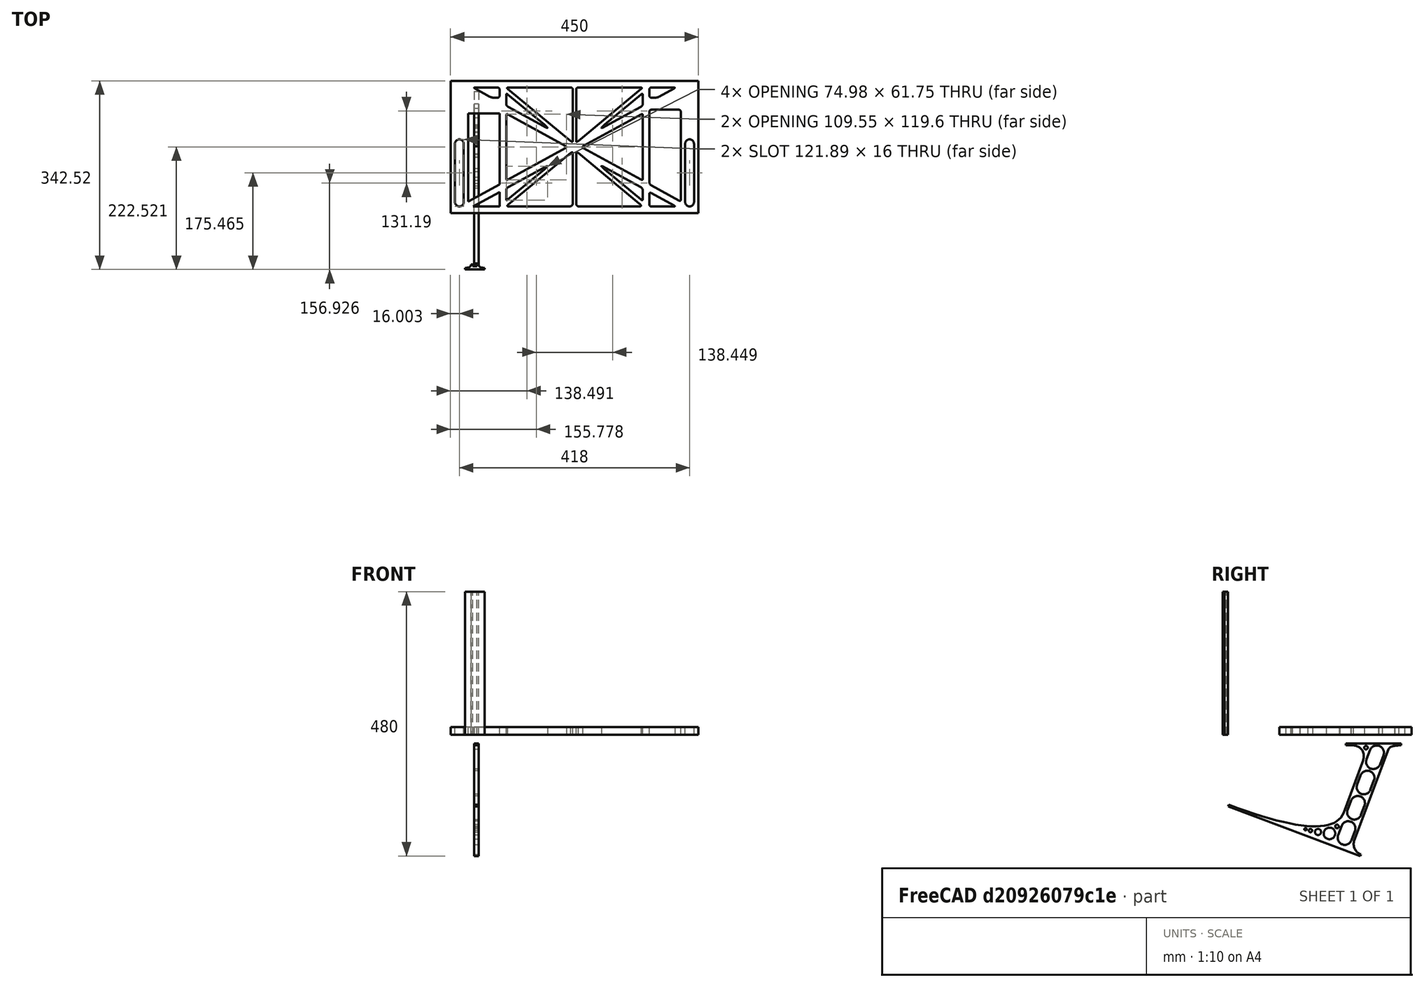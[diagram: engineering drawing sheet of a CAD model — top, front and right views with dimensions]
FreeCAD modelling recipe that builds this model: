
FCSTD DOCUMENT  (FreeCAD 0.19R0.19.2)
Label: laptopStand120FCStd
License: All rights reserved
LicenseURL: http://en.wikipedia.org/wiki/All_rights_reserved
objects: Sketcher::SketchObject×3, Part::Extrusion×3
note: 6 computed .brp shape members not serialized (recipe doc carries the construction recipe); baked Part::Feature solids carry a one-line shape summary decoded from their .brp

FEATURE [Sketcher::SketchObject] Sketch
  FullyConstrained = false
  sketch-geometry (339):
    g0: LineSegment StartX=-10.9272 StartY=-82.7794 StartZ=0 EndX=46.0728 EndY=-51.4823 EndZ=0
    g1: LineSegment StartX=-10.9272 StartY=77.3346 StartZ=0 EndX=-10.9272 EndY=-82.7794 EndZ=0
    g2: LineSegment StartX=-1.92719 StartY=-91.7794 StartZ=0 EndX=46.0728 EndY=-91.7794 EndZ=0
    g3: LineSegment StartX=46.0728 StartY=-65.424 StartZ=0 EndX=-1.92719 EndY=-91.7794 EndZ=0
    g4: LineSegment StartX=46.0728 StartY=-65.424 StartZ=0 EndX=46.0728 EndY=-91.7794 EndZ=0
    g5: LineSegment StartX=46.0728 StartY=77.3346 StartZ=0 EndX=46.0728 EndY=-51.4823 EndZ=0
    g6: LineSegment StartX=-42.9272 StartY=136.221 StartZ=0 EndX=-42.9272 EndY=-103.779 EndZ=0
    g7: LineSegment StartX=407.073 StartY=136.221 StartZ=0 EndX=407.073 EndY=-103.779 EndZ=0
    g8: ArcOfCircle CenterX=-26.9272 CenterY=22.1087 CenterZ=0 NormalX=0 NormalY=0 NormalZ=1 AngleXU=0 Radius=8 StartAngle=1e-16 EndAngle=3.14159
    g9: ArcOfCircle CenterX=-26.9272 CenterY=-83.7794 CenterZ=0 NormalX=0 NormalY=0 NormalZ=1 AngleXU=0 Radius=8 StartAngle=3.14159 EndAngle=6.28319
    g10: LineSegment StartX=-34.9272 StartY=22.1087 StartZ=0 EndX=-34.9272 EndY=-83.7794 EndZ=0
    g11: LineSegment StartX=-18.9272 StartY=22.1087 StartZ=0 EndX=-18.9272 EndY=-83.7794 EndZ=0
    g12: ArcOfCircle CenterX=391.073 CenterY=22.1087 CenterZ=0 NormalX=0 NormalY=0 NormalZ=1 AngleXU=0 Radius=8 StartAngle=-4.4e-15 EndAngle=3.14159
    g13: LineSegment StartX=399.073 StartY=22.1087 StartZ=0 EndX=399.073 EndY=-83.7794 EndZ=0
    g14: LineSegment StartX=383.073 StartY=22.1087 StartZ=0 EndX=383.073 EndY=-83.7794 EndZ=0
    g15: ArcOfCircle CenterX=391.073 CenterY=-83.7794 CenterZ=0 NormalX=0 NormalY=0 NormalZ=1 AngleXU=0 Radius=8 StartAngle=3.14159 EndAngle=6.28319
    g16: Circle CenterX=175.022 CenterY=27.0628 CenterZ=0 NormalX=0 NormalY=0 NormalZ=1 AngleXU=0 Radius=1
    g17: Circle CenterX=179.022 CenterY=24.8665 CenterZ=0 NormalX=0 NormalY=0 NormalZ=1 AngleXU=0 Radius=1
    g18: Circle CenterX=179.022 CenterY=27.0628 CenterZ=0 NormalX=0 NormalY=0 NormalZ=1 AngleXU=0 Radius=1
    g19: BSplineCurve PolesCount=3 KnotsCount=2 Degree=2 IsPeriodic=0
    g20: GeomPoint X=175.022 Y=27.0628 Z=0
    g21: GeomPoint X=179.022 Y=27.0628 Z=0
    g22: Circle CenterX=189.124 CenterY=27.0628 CenterZ=0 NormalX=0 NormalY=0 NormalZ=1 AngleXU=0 Radius=1
    g23: Circle CenterX=185.124 CenterY=24.8665 CenterZ=0 NormalX=0 NormalY=0 NormalZ=1 AngleXU=0 Radius=1
    g24: Circle CenterX=185.124 CenterY=27.0628 CenterZ=0 NormalX=0 NormalY=0 NormalZ=1 AngleXU=0 Radius=1
    g25: BSplineCurve PolesCount=3 KnotsCount=2 Degree=2 IsPeriodic=0
    g26: GeomPoint X=189.124 Y=27.0628 Z=0
    g27: GeomPoint X=185.124 Y=27.0628 Z=0
    g28: Circle CenterX=175.022 CenterY=5.37834 CenterZ=0 NormalX=0 NormalY=0 NormalZ=1 AngleXU=0 Radius=1
    g29: Circle CenterX=179.022 CenterY=7.57463 CenterZ=0 NormalX=0 NormalY=0 NormalZ=1 AngleXU=0 Radius=1
    g30: Circle CenterX=179.022 CenterY=5.34704 CenterZ=0 NormalX=0 NormalY=0 NormalZ=1 AngleXU=0 Radius=1
    g31: BSplineCurve PolesCount=3 KnotsCount=2 Degree=2 IsPeriodic=0
    g32: GeomPoint X=175.022 Y=5.37834 Z=0
    g33: GeomPoint X=179.022 Y=5.34704 Z=0
    g34: Circle CenterX=189.124 CenterY=5.37834 CenterZ=0 NormalX=0 NormalY=0 NormalZ=1 AngleXU=0 Radius=1
    g35: Circle CenterX=185.124 CenterY=7.57463 CenterZ=0 NormalX=0 NormalY=0 NormalZ=1 AngleXU=0 Radius=1
    g36: Circle CenterX=185.124 CenterY=5.34704 CenterZ=0 NormalX=0 NormalY=0 NormalZ=1 AngleXU=0 Radius=1
    g37: BSplineCurve PolesCount=3 KnotsCount=2 Degree=2 IsPeriodic=0
    g38: GeomPoint X=189.124 Y=5.37834 Z=0
    g39: GeomPoint X=185.124 Y=5.34704 Z=0
    g40: Circle CenterX=165.871 CenterY=18.1458 CenterZ=0 NormalX=0 NormalY=0 NormalZ=1 AngleXU=0 Radius=1
    g41: Circle CenterX=169.377 CenterY=16.2206 CenterZ=0 NormalX=0 NormalY=0 NormalZ=1 AngleXU=0 Radius=1
    g42: Circle CenterX=165.871 CenterY=14.2954 CenterZ=0 NormalX=0 NormalY=0 NormalZ=1 AngleXU=0 Radius=1
    g43: BSplineCurve PolesCount=3 KnotsCount=2 Degree=2 IsPeriodic=0
    g44: GeomPoint X=165.871 Y=18.1458 Z=0
    g45: GeomPoint X=165.871 Y=14.2954 Z=0
    g46: Circle CenterX=198.275 CenterY=18.1458 CenterZ=0 NormalX=0 NormalY=0 NormalZ=1 AngleXU=0 Radius=1
    g47: Circle CenterX=194.768 CenterY=16.2206 CenterZ=0 NormalX=0 NormalY=0 NormalZ=1 AngleXU=0 Radius=1
    g48: Circle CenterX=198.275 CenterY=14.2954 CenterZ=0 NormalX=0 NormalY=0 NormalZ=1 AngleXU=0 Radius=1
    g49: BSplineCurve PolesCount=3 KnotsCount=2 Degree=2 IsPeriodic=0
    g50: GeomPoint X=198.275 Y=18.1458 Z=0
    g51: GeomPoint X=198.275 Y=14.2954 Z=0
    g52: LineSegment StartX=407.073 StartY=-103.779 StartZ=0 EndX=-42.9272 EndY=-103.779 EndZ=0
    g53: LineSegment StartX=407.073 StartY=136.221 StartZ=0 EndX=-42.9272 EndY=136.221 EndZ=0
    g54: LineSegment StartX=46.0728 StartY=77.3346 StartZ=0 EndX=-10.9272 EndY=77.3346 EndZ=0
    g55: Circle CenterX=125.607 CenterY=54.1951 CenterZ=0 NormalX=0 NormalY=0 NormalZ=1 AngleXU=0 Radius=1
    g56: Circle CenterX=139.632 CenterY=46.4944 CenterZ=0 NormalX=0 NormalY=0 NormalZ=1 AngleXU=0 Radius=1
    g57: Circle CenterX=127.326 CenterY=56.7187 CenterZ=0 NormalX=0 NormalY=0 NormalZ=1 AngleXU=0 Radius=1
    g58: BSplineCurve PolesCount=3 KnotsCount=2 Degree=2 IsPeriodic=0
    g59: GeomPoint X=125.607 Y=54.1951 Z=0
    g60: GeomPoint X=127.326 Y=56.7187 Z=0
    g61: Circle CenterX=236.821 CenterY=56.7187 CenterZ=0 NormalX=0 NormalY=0 NormalZ=1 AngleXU=0 Radius=1
    g62: Circle CenterX=224.513 CenterY=46.4944 CenterZ=0 NormalX=0 NormalY=0 NormalZ=1 AngleXU=0 Radius=1
    g63: Circle CenterX=238.538 CenterY=54.1951 CenterZ=0 NormalX=0 NormalY=0 NormalZ=1 AngleXU=0 Radius=1
    g64: BSplineCurve PolesCount=3 KnotsCount=2 Degree=2 IsPeriodic=0
    g65: GeomPoint X=236.821 Y=56.7187 Z=0
    g66: GeomPoint X=238.538 Y=54.1951 Z=0
    g67: Circle CenterX=238.538 CenterY=-21.7539 CenterZ=0 NormalX=0 NormalY=0 NormalZ=1 AngleXU=0 Radius=1
    g68: Circle CenterX=224.513 CenterY=-14.0532 CenterZ=0 NormalX=0 NormalY=0 NormalZ=1 AngleXU=0 Radius=1
    g69: Circle CenterX=236.821 CenterY=-24.2775 CenterZ=0 NormalX=0 NormalY=0 NormalZ=1 AngleXU=0 Radius=1
    g70: BSplineCurve PolesCount=3 KnotsCount=2 Degree=2 IsPeriodic=0
    g71: GeomPoint X=238.538 Y=-21.7539 Z=0
    g72: GeomPoint X=236.821 Y=-24.2775 Z=0
    g73: Circle CenterX=125.607 CenterY=-21.7539 CenterZ=0 NormalX=0 NormalY=0 NormalZ=1 AngleXU=0 Radius=1
    g74: Circle CenterX=139.632 CenterY=-14.0532 CenterZ=0 NormalX=0 NormalY=0 NormalZ=1 AngleXU=0 Radius=1
    g75: Circle CenterX=127.325 CenterY=-24.2775 CenterZ=0 NormalX=0 NormalY=0 NormalZ=1 AngleXU=0 Radius=1
    g76: BSplineCurve PolesCount=3 KnotsCount=2 Degree=2 IsPeriodic=0
    g77: GeomPoint X=125.607 Y=-21.7539 Z=0
    g78: GeomPoint X=127.325 Y=-24.2775 Z=0
    g79: Circle CenterX=302.996 CenterY=111.695 CenterZ=0 NormalX=0 NormalY=0 NormalZ=1 AngleXU=0 Radius=1
    g80: Circle CenterX=306.073 CenterY=114.251 CenterZ=0 NormalX=0 NormalY=0 NormalZ=1 AngleXU=0 Radius=1
    g81: Circle CenterX=306.073 CenterY=110.251 CenterZ=0 NormalX=0 NormalY=0 NormalZ=1 AngleXU=0 Radius=1
    g82: BSplineCurve PolesCount=3 KnotsCount=2 Degree=2 IsPeriodic=0
    g83: GeomPoint X=302.996 Y=111.695 Z=0
    g84: GeomPoint X=306.073 Y=110.251 Z=0
    g85: Circle CenterX=306.073 CenterY=95.2763 CenterZ=0 NormalX=0 NormalY=0 NormalZ=1 AngleXU=0 Radius=1
    g86: Circle CenterX=306.073 CenterY=91.2763 CenterZ=0 NormalX=0 NormalY=0 NormalZ=1 AngleXU=0 Radius=1
    g87: Circle CenterX=302.567 CenterY=89.3511 CenterZ=0 NormalX=0 NormalY=0 NormalZ=1 AngleXU=0 Radius=1
    g88: BSplineCurve PolesCount=3 KnotsCount=2 Degree=2 IsPeriodic=0
    g89: GeomPoint X=306.073 Y=95.2763 Z=0
    g90: GeomPoint X=302.567 Y=89.3511 Z=0
    g91: LineSegment StartX=306.073 StartY=110.251 StartZ=0 EndX=306.073 EndY=95.2763 EndZ=0
    g92: LineSegment StartX=302.996 StartY=111.695 StartZ=0 EndX=236.821 EndY=56.7187 EndZ=0
    g93: LineSegment StartX=238.538 StartY=54.1951 StartZ=0 EndX=302.567 EndY=89.3511 EndZ=0
    g94: Circle CenterX=61.1496 CenterY=111.695 CenterZ=0 NormalX=0 NormalY=0 NormalZ=1 AngleXU=0 Radius=1
    g95: Circle CenterX=58.0728 CenterY=114.251 CenterZ=0 NormalX=0 NormalY=0 NormalZ=1 AngleXU=0 Radius=1
    g96: Circle CenterX=58.0728 CenterY=110.251 CenterZ=0 NormalX=0 NormalY=0 NormalZ=1 AngleXU=0 Radius=1
    g97: BSplineCurve PolesCount=3 KnotsCount=2 Degree=2 IsPeriodic=0
    g98: GeomPoint X=61.1496 Y=111.695 Z=0
    g99: GeomPoint X=58.0728 Y=110.251 Z=0
    g100: Circle CenterX=61.5791 CenterY=89.3511 CenterZ=0 NormalX=0 NormalY=0 NormalZ=1 AngleXU=0 Radius=1
    g101: Circle CenterX=58.0728 CenterY=91.2763 CenterZ=0 NormalX=0 NormalY=0 NormalZ=1 AngleXU=0 Radius=1
    g102: Circle CenterX=58.0728 CenterY=95.2763 CenterZ=0 NormalX=0 NormalY=0 NormalZ=1 AngleXU=0 Radius=1
    g103: BSplineCurve PolesCount=3 KnotsCount=2 Degree=2 IsPeriodic=0
    g104: GeomPoint X=61.5791 Y=89.3511 Z=0
    g105: GeomPoint X=58.0728 Y=95.2763 Z=0
    g106: LineSegment StartX=58.0728 StartY=110.251 StartZ=0 EndX=58.0728 EndY=95.2763 EndZ=0
    g107: LineSegment StartX=61.1496 StartY=111.695 StartZ=0 EndX=127.326 EndY=56.7187 EndZ=0
    g108: LineSegment StartX=125.607 StartY=54.1951 StartZ=0 EndX=61.5791 EndY=89.3511 EndZ=0
    g109: Circle CenterX=61.5791 CenterY=-56.9099 CenterZ=0 NormalX=0 NormalY=0 NormalZ=1 AngleXU=0 Radius=1
    g110: Circle CenterX=58.0728 CenterY=-58.8351 CenterZ=0 NormalX=0 NormalY=0 NormalZ=1 AngleXU=0 Radius=1
    g111: Circle CenterX=58.0728 CenterY=-62.8351 CenterZ=0 NormalX=0 NormalY=0 NormalZ=1 AngleXU=0 Radius=1
    g112: BSplineCurve PolesCount=3 KnotsCount=2 Degree=2 IsPeriodic=0
    g113: GeomPoint X=61.5791 Y=-56.9099 Z=0
    g114: GeomPoint X=58.0728 Y=-62.8351 Z=0
    g115: Circle CenterX=58.0728 CenterY=-77.8102 CenterZ=0 NormalX=0 NormalY=0 NormalZ=1 AngleXU=0 Radius=1
    g116: Circle CenterX=58.0728 CenterY=-81.8102 CenterZ=0 NormalX=0 NormalY=0 NormalZ=1 AngleXU=0 Radius=1
    g117: Circle CenterX=61.1496 CenterY=-79.2541 CenterZ=0 NormalX=0 NormalY=0 NormalZ=1 AngleXU=0 Radius=1
    g118: BSplineCurve PolesCount=3 KnotsCount=2 Degree=2 IsPeriodic=0
    g119: GeomPoint X=58.0728 Y=-77.8102 Z=0
    g120: GeomPoint X=61.1496 Y=-79.2541 Z=0
    g121: LineSegment StartX=58.0728 StartY=-62.8351 StartZ=0 EndX=58.0728 EndY=-77.8102 EndZ=0
    g122: LineSegment StartX=61.1496 StartY=-79.2541 StartZ=0 EndX=127.325 EndY=-24.2775 EndZ=0
    g123: LineSegment StartX=125.607 StartY=-21.7539 StartZ=0 EndX=61.5791 EndY=-56.9099 EndZ=0
    g124: Circle CenterX=302.567 CenterY=-56.9099 CenterZ=0 NormalX=0 NormalY=0 NormalZ=1 AngleXU=0 Radius=1
    g125: Circle CenterX=306.073 CenterY=-58.8351 CenterZ=0 NormalX=0 NormalY=0 NormalZ=1 AngleXU=0 Radius=1
    g126: Circle CenterX=306.073 CenterY=-62.8351 CenterZ=0 NormalX=0 NormalY=0 NormalZ=1 AngleXU=0 Radius=1
    g127: BSplineCurve PolesCount=3 KnotsCount=2 Degree=2 IsPeriodic=0
    g128: GeomPoint X=302.567 Y=-56.9099 Z=0
    g129: GeomPoint X=306.073 Y=-62.8351 Z=0
    g130: Circle CenterX=302.996 CenterY=-79.2541 CenterZ=0 NormalX=0 NormalY=0 NormalZ=1 AngleXU=0 Radius=1
    g131: Circle CenterX=306.073 CenterY=-81.8102 CenterZ=0 NormalX=0 NormalY=0 NormalZ=1 AngleXU=0 Radius=1
    g132: Circle CenterX=306.073 CenterY=-77.8102 CenterZ=0 NormalX=0 NormalY=0 NormalZ=1 AngleXU=0 Radius=1
    g133: BSplineCurve PolesCount=3 KnotsCount=2 Degree=2 IsPeriodic=0
    g134: GeomPoint X=302.996 Y=-79.2541 Z=0
    g135: GeomPoint X=306.073 Y=-77.8102 Z=0
    g136: LineSegment StartX=306.073 StartY=-62.8351 StartZ=0 EndX=306.073 EndY=-77.8102 EndZ=0
    g137: LineSegment StartX=302.996 StartY=-79.2541 StartZ=0 EndX=236.821 EndY=-24.2775 EndZ=0
    g138: LineSegment StartX=238.538 StartY=-21.7539 StartZ=0 EndX=302.567 EndY=-56.9099 EndZ=0
    g139: Circle CenterX=61.6457 CenterY=-88.8112 CenterZ=0 NormalX=0 NormalY=0 NormalZ=1 AngleXU=0 Radius=1
    g140: Circle CenterX=58.0728 CenterY=-91.7794 CenterZ=0 NormalX=0 NormalY=0 NormalZ=1 AngleXU=0 Radius=1
    g141: Circle CenterX=63.9135 CenterY=-91.7794 CenterZ=0 NormalX=0 NormalY=0 NormalZ=1 AngleXU=0 Radius=1
    g142: BSplineCurve PolesCount=3 KnotsCount=2 Degree=2 IsPeriodic=0
    g143: GeomPoint X=61.6457 Y=-88.8112 Z=0
    g144: GeomPoint X=63.9135 Y=-91.7794 Z=0
    g145: Circle CenterX=179.022 CenterY=-85.8163 CenterZ=0 NormalX=0 NormalY=0 NormalZ=1 AngleXU=0 Radius=1
    g146: Circle CenterX=179.022 CenterY=-91.7794 CenterZ=0 NormalX=0 NormalY=0 NormalZ=1 AngleXU=0 Radius=1
    g147: Circle CenterX=171.895 CenterY=-91.7794 CenterZ=0 NormalX=0 NormalY=0 NormalZ=1 AngleXU=0 Radius=1
    g148: BSplineCurve PolesCount=3 KnotsCount=2 Degree=2 IsPeriodic=0
    g149: GeomPoint X=179.022 Y=-85.8163 Z=0
    g150: GeomPoint X=171.895 Y=-91.7794 Z=0
    g151: Circle CenterX=185.124 CenterY=-86.2028 CenterZ=0 NormalX=0 NormalY=0 NormalZ=1 AngleXU=0 Radius=1
    g152: Circle CenterX=185.124 CenterY=-91.7794 CenterZ=0 NormalX=0 NormalY=0 NormalZ=1 AngleXU=0 Radius=1
    g153: Circle CenterX=191.747 CenterY=-91.7794 CenterZ=0 NormalX=0 NormalY=0 NormalZ=1 AngleXU=0 Radius=1
    g154: BSplineCurve PolesCount=3 KnotsCount=2 Degree=2 IsPeriodic=0
    g155: GeomPoint X=185.124 Y=-86.2028 Z=0
    g156: GeomPoint X=191.747 Y=-91.7794 Z=0
    g157: Circle CenterX=299.888 CenterY=-86.6413 CenterZ=0 NormalX=0 NormalY=0 NormalZ=1 AngleXU=0 Radius=1
    g158: Circle CenterX=306.073 CenterY=-91.7794 CenterZ=0 NormalX=0 NormalY=0 NormalZ=1 AngleXU=0 Radius=1
    g159: Circle CenterX=298.776 CenterY=-91.7794 CenterZ=0 NormalX=0 NormalY=0 NormalZ=1 AngleXU=0 Radius=1
    g160: BSplineCurve PolesCount=3 KnotsCount=2 Degree=2 IsPeriodic=0
    g161: GeomPoint X=299.888 Y=-86.6413 Z=0
    g162: GeomPoint X=298.776 Y=-91.7794 Z=0
    g163: LineSegment StartX=189.124 StartY=5.37834 StartZ=0 EndX=299.888 EndY=-86.6413 EndZ=0
    g164: LineSegment StartX=298.776 StartY=-91.7794 StartZ=0 EndX=191.747 EndY=-91.7794 EndZ=0
    g165: LineSegment StartX=185.124 StartY=-86.2028 StartZ=0 EndX=185.124 EndY=5.34704 EndZ=0
    g166: LineSegment StartX=179.022 StartY=5.34704 StartZ=0 EndX=179.022 EndY=-85.8163 EndZ=0
    g167: LineSegment StartX=171.895 StartY=-91.7794 StartZ=0 EndX=63.9135 EndY=-91.7794 EndZ=0
    g168: LineSegment StartX=61.6457 StartY=-88.8112 StartZ=0 EndX=175.022 EndY=5.37834 EndZ=0
    g169: Circle CenterX=302.073 CenterY=124.221 CenterZ=0 NormalX=0 NormalY=0 NormalZ=1 AngleXU=0 Radius=1
    g170: Circle CenterX=306.073 CenterY=124.221 CenterZ=0 NormalX=0 NormalY=0 NormalZ=1 AngleXU=0 Radius=1
    g171: Circle CenterX=302.996 CenterY=121.665 CenterZ=0 NormalX=0 NormalY=0 NormalZ=1 AngleXU=0 Radius=1
    g172: BSplineCurve PolesCount=3 KnotsCount=2 Degree=2 IsPeriodic=0
    g173: GeomPoint X=302.073 Y=124.221 Z=0
    g174: GeomPoint X=302.996 Y=121.665 Z=0
    g175: Circle CenterX=189.124 CenterY=124.221 CenterZ=0 NormalX=0 NormalY=0 NormalZ=1 AngleXU=0 Radius=1
    g176: Circle CenterX=185.124 CenterY=124.221 CenterZ=0 NormalX=0 NormalY=0 NormalZ=1 AngleXU=0 Radius=1
    g177: Circle CenterX=185.124 CenterY=120.221 CenterZ=0 NormalX=0 NormalY=0 NormalZ=1 AngleXU=0 Radius=1
    g178: BSplineCurve PolesCount=3 KnotsCount=2 Degree=2 IsPeriodic=0
    g179: GeomPoint X=189.124 Y=124.221 Z=0
    g180: GeomPoint X=185.124 Y=120.221 Z=0
    g181: Circle CenterX=175.022 CenterY=124.221 CenterZ=0 NormalX=0 NormalY=0 NormalZ=1 AngleXU=0 Radius=1
    g182: Circle CenterX=179.022 CenterY=124.221 CenterZ=0 NormalX=0 NormalY=0 NormalZ=1 AngleXU=0 Radius=1
    g183: Circle CenterX=179.022 CenterY=120.221 CenterZ=0 NormalX=0 NormalY=0 NormalZ=1 AngleXU=0 Radius=1
    g184: BSplineCurve PolesCount=3 KnotsCount=2 Degree=2 IsPeriodic=0
    g185: GeomPoint X=175.022 Y=124.221 Z=0
    g186: GeomPoint X=179.022 Y=120.221 Z=0
    g187: Circle CenterX=62.0728 CenterY=124.221 CenterZ=0 NormalX=0 NormalY=0 NormalZ=1 AngleXU=0 Radius=1
    g188: Circle CenterX=58.0728 CenterY=124.221 CenterZ=0 NormalX=0 NormalY=0 NormalZ=1 AngleXU=0 Radius=1
    g189: Circle CenterX=61.1496 CenterY=121.665 CenterZ=0 NormalX=0 NormalY=0 NormalZ=1 AngleXU=0 Radius=1
    g190: BSplineCurve PolesCount=3 KnotsCount=2 Degree=2 IsPeriodic=0
    g191: GeomPoint X=62.0728 Y=124.221 Z=0
    g192: GeomPoint X=61.1496 Y=121.665 Z=0
    g193: LineSegment StartX=62.0728 StartY=124.221 StartZ=0 EndX=175.022 EndY=124.221 EndZ=0
    g194: LineSegment StartX=179.022 StartY=120.221 StartZ=0 EndX=179.022 EndY=27.0628 EndZ=0
    g195: LineSegment StartX=185.124 StartY=27.0628 StartZ=0 EndX=185.124 EndY=120.221 EndZ=0
    g196: LineSegment StartX=189.124 StartY=124.221 StartZ=0 EndX=302.073 EndY=124.221 EndZ=0
    g197: LineSegment StartX=302.996 StartY=121.665 StartZ=0 EndX=189.124 EndY=27.0628 EndZ=0
    g198: LineSegment StartX=175.022 StartY=27.0628 StartZ=0 EndX=61.1496 EndY=121.665 EndZ=0
    g199: Circle CenterX=61.5791 CenterY=75.4095 CenterZ=0 NormalX=0 NormalY=0 NormalZ=1 AngleXU=0 Radius=1
    g200: Circle CenterX=58.0728 CenterY=77.3346 CenterZ=0 NormalX=0 NormalY=0 NormalZ=1 AngleXU=0 Radius=1
    g201: Circle CenterX=58.0728 CenterY=73.3346 CenterZ=0 NormalX=0 NormalY=0 NormalZ=1 AngleXU=0 Radius=1
    g202: BSplineCurve PolesCount=3 KnotsCount=2 Degree=2 IsPeriodic=0
    g203: GeomPoint X=61.5791 Y=75.4095 Z=0
    g204: GeomPoint X=58.0728 Y=73.3346 Z=0
    g205: Circle CenterX=58.0728 CenterY=-40.8935 CenterZ=0 NormalX=0 NormalY=0 NormalZ=1 AngleXU=0 Radius=1
    g206: Circle CenterX=58.0728 CenterY=-44.8935 CenterZ=0 NormalX=0 NormalY=0 NormalZ=1 AngleXU=0 Radius=1
    g207: Circle CenterX=61.5791 CenterY=-42.9683 CenterZ=0 NormalX=0 NormalY=0 NormalZ=1 AngleXU=0 Radius=1
    g208: BSplineCurve PolesCount=3 KnotsCount=2 Degree=2 IsPeriodic=0
    g209: GeomPoint X=58.0728 Y=-40.8935 Z=0
    g210: GeomPoint X=61.5791 Y=-42.9683 Z=0
    g211: LineSegment StartX=61.5791 StartY=-42.9683 StartZ=0 EndX=165.871 EndY=14.2954 EndZ=0
    g212: LineSegment StartX=165.871 StartY=18.1458 StartZ=0 EndX=61.5791 EndY=75.4095 EndZ=0
    g213: LineSegment StartX=58.0728 StartY=73.3346 StartZ=0 EndX=58.0728 EndY=-40.8935 EndZ=0
    g214: Circle CenterX=302.567 CenterY=-42.9683 CenterZ=0 NormalX=0 NormalY=0 NormalZ=1 AngleXU=0 Radius=1
    g215: Circle CenterX=306.073 CenterY=-44.8935 CenterZ=0 NormalX=0 NormalY=0 NormalZ=1 AngleXU=0 Radius=1
    g216: Circle CenterX=306.073 CenterY=-40.8935 CenterZ=0 NormalX=0 NormalY=0 NormalZ=1 AngleXU=0 Radius=1
    g217: BSplineCurve PolesCount=3 KnotsCount=2 Degree=2 IsPeriodic=0
    g218: GeomPoint X=302.567 Y=-42.9683 Z=0
    g219: GeomPoint X=306.073 Y=-40.8935 Z=0
    g220: Circle CenterX=306.073 CenterY=73.3346 CenterZ=0 NormalX=0 NormalY=0 NormalZ=1 AngleXU=0 Radius=1
    g221: Circle CenterX=306.073 CenterY=77.3346 CenterZ=0 NormalX=0 NormalY=0 NormalZ=1 AngleXU=0 Radius=1
    g222: Circle CenterX=302.567 CenterY=75.4095 CenterZ=0 NormalX=0 NormalY=0 NormalZ=1 AngleXU=0 Radius=1
    g223: BSplineCurve PolesCount=3 KnotsCount=2 Degree=2 IsPeriodic=0
    g224: GeomPoint X=306.073 Y=73.3346 Z=0
    g225: GeomPoint X=302.567 Y=75.4095 Z=0
    g226: LineSegment StartX=302.567 StartY=-42.9683 StartZ=0 EndX=198.275 EndY=14.2954 EndZ=0
    g227: LineSegment StartX=198.275 StartY=18.1458 StartZ=0 EndX=302.567 EndY=75.4095 EndZ=0
    g228: LineSegment StartX=306.073 StartY=73.3346 StartZ=0 EndX=306.073 EndY=-40.8935 EndZ=0
    g229: LineSegment StartX=322.073 StartY=105.865 StartZ=0 EndX=328.643 EndY=105.865 EndZ=0
    g230: LineSegment StartX=318.073 StartY=120.221 StartZ=0 EndX=318.073 EndY=109.865 EndZ=0
    g231: LineSegment StartX=336.157 StartY=107.779 StartZ=0 EndX=362.567 EndY=122.294 EndZ=0
    g232: Circle CenterX=362.073 CenterY=124.221 CenterZ=0 NormalX=0 NormalY=0 NormalZ=1 AngleXU=0 Radius=1
    g233: Circle CenterX=366.073 CenterY=124.221 CenterZ=0 NormalX=0 NormalY=0 NormalZ=1 AngleXU=0 Radius=1
    g234: Circle CenterX=362.567 CenterY=122.294 CenterZ=0 NormalX=0 NormalY=0 NormalZ=1 AngleXU=0 Radius=1
    g235: BSplineCurve PolesCount=3 KnotsCount=2 Degree=2 IsPeriodic=0
    g236: GeomPoint X=362.073 Y=124.221 Z=0
    g237: GeomPoint X=362.567 Y=122.294 Z=0
    g238: Circle CenterX=322.073 CenterY=124.221 CenterZ=0 NormalX=0 NormalY=0 NormalZ=1 AngleXU=0 Radius=1
    g239: Circle CenterX=318.073 CenterY=124.221 CenterZ=0 NormalX=0 NormalY=0 NormalZ=1 AngleXU=0 Radius=1
    g240: Circle CenterX=318.073 CenterY=120.221 CenterZ=0 NormalX=0 NormalY=0 NormalZ=1 AngleXU=0 Radius=1
    g241: BSplineCurve PolesCount=3 KnotsCount=2 Degree=2 IsPeriodic=0
    g242: GeomPoint X=322.073 Y=124.221 Z=0
    g243: GeomPoint X=318.073 Y=120.221 Z=0
    g244: Circle CenterX=322.073 CenterY=105.865 CenterZ=0 NormalX=0 NormalY=0 NormalZ=1 AngleXU=0 Radius=1
    g245: Circle CenterX=318.073 CenterY=105.865 CenterZ=0 NormalX=0 NormalY=0 NormalZ=1 AngleXU=0 Radius=1
    g246: Circle CenterX=318.073 CenterY=109.865 CenterZ=0 NormalX=0 NormalY=0 NormalZ=1 AngleXU=0 Radius=1
    g247: BSplineCurve PolesCount=3 KnotsCount=2 Degree=2 IsPeriodic=0
    g248: GeomPoint X=322.073 Y=105.865 Z=0
    g249: GeomPoint X=318.073 Y=109.865 Z=0
    g250: Circle CenterX=336.157 CenterY=107.779 CenterZ=0 NormalX=0 NormalY=0 NormalZ=1 AngleXU=0 Radius=1
    g251: Circle CenterX=332.651 CenterY=105.853 CenterZ=0 NormalX=0 NormalY=0 NormalZ=1 AngleXU=0 Radius=1
    g252: Circle CenterX=328.643 CenterY=105.865 CenterZ=0 NormalX=0 NormalY=0 NormalZ=1 AngleXU=0 Radius=1
    g253: BSplineCurve PolesCount=3 KnotsCount=2 Degree=2 IsPeriodic=0
    g254: GeomPoint X=336.157 Y=107.779 Z=0
    g255: GeomPoint X=328.643 Y=105.865 Z=0
    g256: LineSegment StartX=322.073 StartY=124.221 StartZ=0 EndX=362.073 EndY=124.221 EndZ=0
    g257: Circle CenterX=371.567 CenterY=-80.8644 CenterZ=0 NormalX=0 NormalY=0 NormalZ=1 AngleXU=0 Radius=1
    g258: Circle CenterX=375.073 CenterY=-82.7896 CenterZ=0 NormalX=0 NormalY=0 NormalZ=1 AngleXU=0 Radius=1
    g259: Circle CenterX=375.073 CenterY=-78.7896 CenterZ=0 NormalX=0 NormalY=0 NormalZ=1 AngleXU=0 Radius=1
    g260: BSplineCurve PolesCount=3 KnotsCount=2 Degree=2 IsPeriodic=0
    g261: GeomPoint X=371.567 Y=-80.8644 Z=0
    g262: GeomPoint X=375.073 Y=-78.7896 Z=0
    g263: Circle CenterX=321.579 CenterY=-53.4075 CenterZ=0 NormalX=0 NormalY=0 NormalZ=1 AngleXU=0 Radius=1
    g264: Circle CenterX=318.073 CenterY=-51.4823 CenterZ=0 NormalX=0 NormalY=0 NormalZ=1 AngleXU=0 Radius=1
    g265: Circle CenterX=318.073 CenterY=-47.4823 CenterZ=0 NormalX=0 NormalY=0 NormalZ=1 AngleXU=0 Radius=1
    g266: BSplineCurve PolesCount=3 KnotsCount=2 Degree=2 IsPeriodic=0
    g267: GeomPoint X=321.579 Y=-53.4075 Z=0
    g268: GeomPoint X=318.073 Y=-47.4823 Z=0
    g269: Circle CenterX=318.073 CenterY=79.9235 CenterZ=0 NormalX=0 NormalY=0 NormalZ=1 AngleXU=0 Radius=1
    g270: Circle CenterX=318.073 CenterY=83.9235 CenterZ=0 NormalX=0 NormalY=0 NormalZ=1 AngleXU=0 Radius=1
    g271: Circle CenterX=322.073 CenterY=83.9235 CenterZ=0 NormalX=0 NormalY=0 NormalZ=1 AngleXU=0 Radius=1
    g272: BSplineCurve PolesCount=3 KnotsCount=2 Degree=2 IsPeriodic=0
    g273: GeomPoint X=318.073 Y=79.9235 Z=0
    g274: GeomPoint X=322.073 Y=83.9235 Z=0
    g275: Circle CenterX=375.073 CenterY=79.9235 CenterZ=0 NormalX=0 NormalY=0 NormalZ=1 AngleXU=0 Radius=1
    g276: Circle CenterX=375.073 CenterY=83.9235 CenterZ=0 NormalX=0 NormalY=0 NormalZ=1 AngleXU=0 Radius=1
    g277: Circle CenterX=371.073 CenterY=83.9235 CenterZ=0 NormalX=0 NormalY=0 NormalZ=1 AngleXU=0 Radius=1
    g278: BSplineCurve PolesCount=3 KnotsCount=2 Degree=2 IsPeriodic=0
    g279: GeomPoint X=375.073 Y=79.9235 Z=0
    g280: GeomPoint X=371.073 Y=83.9235 Z=0
    g281: LineSegment StartX=322.073 StartY=83.9235 StartZ=0 EndX=371.073 EndY=83.9235 EndZ=0
    g282: LineSegment StartX=375.073 StartY=79.9235 StartZ=0 EndX=375.073 EndY=-78.7896 EndZ=0
    g283: LineSegment StartX=371.567 StartY=-80.8644 StartZ=0 EndX=321.579 EndY=-53.4075 EndZ=0
    g284: LineSegment StartX=318.073 StartY=-47.4823 StartZ=0 EndX=318.073 EndY=79.9235 EndZ=0
    g285: Circle CenterX=321.579 CenterY=-67.3492 CenterZ=0 NormalX=0 NormalY=0 NormalZ=1 AngleXU=0 Radius=1
    g286: Circle CenterX=318.073 CenterY=-65.424 CenterZ=0 NormalX=0 NormalY=0 NormalZ=1 AngleXU=0 Radius=1
    g287: Circle CenterX=318.073 CenterY=-69.424 CenterZ=0 NormalX=0 NormalY=0 NormalZ=1 AngleXU=0 Radius=1
    g288: BSplineCurve PolesCount=3 KnotsCount=2 Degree=2 IsPeriodic=0
    g289: GeomPoint X=321.579 Y=-67.3492 Z=0
    g290: GeomPoint X=318.073 Y=-69.424 Z=0
    g291: Circle CenterX=362.567 CenterY=-89.8542 CenterZ=0 NormalX=0 NormalY=0 NormalZ=1 AngleXU=0 Radius=1
    g292: Circle CenterX=366.073 CenterY=-91.7794 CenterZ=0 NormalX=0 NormalY=0 NormalZ=1 AngleXU=0 Radius=1
    g293: Circle CenterX=362.073 CenterY=-91.7794 CenterZ=0 NormalX=0 NormalY=0 NormalZ=1 AngleXU=0 Radius=1
    g294: BSplineCurve PolesCount=3 KnotsCount=2 Degree=2 IsPeriodic=0
    g295: GeomPoint X=362.567 Y=-89.8542 Z=0
    g296: GeomPoint X=362.073 Y=-91.7794 Z=0
    g297: Circle CenterX=322.073 CenterY=-91.7794 CenterZ=0 NormalX=0 NormalY=0 NormalZ=1 AngleXU=0 Radius=1
    g298: Circle CenterX=318.073 CenterY=-91.7794 CenterZ=0 NormalX=0 NormalY=0 NormalZ=1 AngleXU=0 Radius=1
    g299: Circle CenterX=318.073 CenterY=-87.7794 CenterZ=0 NormalX=0 NormalY=0 NormalZ=1 AngleXU=0 Radius=1
    g300: BSplineCurve PolesCount=3 KnotsCount=2 Degree=2 IsPeriodic=0
    g301: GeomPoint X=322.073 Y=-91.7794 Z=0
    g302: GeomPoint X=318.073 Y=-87.7794 Z=0
    g303: LineSegment StartX=362.567 StartY=-89.8542 StartZ=0 EndX=321.579 EndY=-67.3492 EndZ=0
    g304: LineSegment StartX=318.073 StartY=-69.424 StartZ=0 EndX=318.073 EndY=-87.7794 EndZ=0
    g305: LineSegment StartX=322.073 StartY=-91.7794 StartZ=0 EndX=362.073 EndY=-91.7794 EndZ=0
    g306: Circle CenterX=2.07281 CenterY=124.221 CenterZ=0 NormalX=0 NormalY=0 NormalZ=1 AngleXU=0 Radius=1
    g307: Circle CenterX=1.57905 CenterY=122.295 CenterZ=0 NormalX=0 NormalY=0 NormalZ=1 AngleXU=0 Radius=1
    g308: BSplineCurve PolesCount=3 KnotsCount=2 Degree=2 IsPeriodic=0
    g309: GeomPoint X=2.07281 Y=124.221 Z=0
    g310: GeomPoint X=1.57905 Y=122.295 Z=0
    g311: Circle CenterX=42.0728 CenterY=124.221 CenterZ=0 NormalX=0 NormalY=0 NormalZ=1 AngleXU=0 Radius=1
    g312: Circle CenterX=46.0728 CenterY=124.221 CenterZ=0 NormalX=0 NormalY=0 NormalZ=1 AngleXU=0 Radius=1
    g313: Circle CenterX=46.0728 CenterY=120.221 CenterZ=0 NormalX=0 NormalY=0 NormalZ=1 AngleXU=0 Radius=1
    g314: BSplineCurve PolesCount=3 KnotsCount=2 Degree=2 IsPeriodic=0
    g315: GeomPoint X=42.0728 Y=124.221 Z=0
    g316: GeomPoint X=46.0728 Y=120.221 Z=0
    g317: Circle CenterX=46.0728 CenterY=109.865 CenterZ=0 NormalX=0 NormalY=0 NormalZ=1 AngleXU=0 Radius=1
    g318: Circle CenterX=46.0728 CenterY=105.865 CenterZ=0 NormalX=0 NormalY=0 NormalZ=1 AngleXU=0 Radius=1
    g319: Circle CenterX=42.0728 CenterY=105.865 CenterZ=0 NormalX=0 NormalY=0 NormalZ=1 AngleXU=0 Radius=1
    g320: BSplineCurve PolesCount=3 KnotsCount=2 Degree=2 IsPeriodic=0
    g321: GeomPoint X=46.0728 Y=109.865 Z=0
    g322: GeomPoint X=42.0728 Y=105.865 Z=0
    g323: Circle CenterX=35.5028 CenterY=105.865 CenterZ=0 NormalX=0 NormalY=0 NormalZ=1 AngleXU=0 Radius=1
    g324: Circle CenterX=31.5028 CenterY=105.865 CenterZ=0 NormalX=0 NormalY=0 NormalZ=1 AngleXU=0 Radius=1
    g325: Circle CenterX=27.9965 CenterY=107.79 CenterZ=0 NormalX=0 NormalY=0 NormalZ=1 AngleXU=0 Radius=1
    g326: BSplineCurve PolesCount=3 KnotsCount=2 Degree=2 IsPeriodic=0
    g327: GeomPoint X=35.5028 Y=105.865 Z=0
    g328: GeomPoint X=27.9965 Y=107.79 Z=0
    g329: LineSegment StartX=2.07281 StartY=124.221 StartZ=0 EndX=42.0728 EndY=124.221 EndZ=0
    g330: LineSegment StartX=46.0728 StartY=120.221 StartZ=0 EndX=46.0728 EndY=109.865 EndZ=0
    g331: LineSegment StartX=42.0728 StartY=105.865 StartZ=0 EndX=35.5028 EndY=105.865 EndZ=0
    g332: LineSegment StartX=27.9965 StartY=107.79 StartZ=0 EndX=1.57905 EndY=122.295 EndZ=0
    g333: LineSegment StartX=47.176 StartY=-65.9989 StartZ=0 EndX=47.176 EndY=-69.9694 EndZ=0
    g334: LineSegment StartX=47.422 StartY=-91.3327 StartZ=0 EndX=47.422 EndY=-86.5189 EndZ=0
    g335: LineSegment StartX=45.1732 StartY=-93.195 StartZ=0 EndX=40.1486 EndY=-93.195 EndZ=0
    g336: LineSegment StartX=-0.926601 StartY=-92.6679 StartZ=0 EndX=3.5358 EndY=-92.6679 EndZ=0
    g337: LineSegment StartX=-1.17256 StartY=-90.5245 StartZ=0 EndX=2.72765 EndY=-88.1352 EndZ=0
    g338: LineSegment StartX=45.2435 StartY=-65.0853 StartZ=0 EndX=41.8703 EndY=-66.8422 EndZ=0
  constraints (556):
    c: Horizontal(g2)
    c: Coincident(g4,g3)
    c: Coincident(g0,g5)
    c: Block(g4)
    c: Block(g3)
    c: Block(g0)
    c: Block(g1)
    c: Block(g2)
    c: Vertical(g6)
    c: Vertical(g7)
    c: Block(g7)
    c: Block(g6)
    c: Tangent(g8,g11) = 1.5708
    c: Tangent(g8,g10) = -1.5708
    c: Tangent(g10,g9) = -1.5708
    c: Tangent(g11,g9) = 1.5708
    c: Vertical(g10)
    c: Equal(g8,g9)
    c: Block(g11)
    c: Block(g10)
    c: Tangent(g12,g13) = 1.5708
    c: Tangent(g13,g15) = 1.5708
    c: Equal(g12,g15)
    c: Coincident(g14,g12)
    c: Coincident(g14,g15)
    c: Block(g13)
    c: Block(g14)
    c: Weight(g16) = 1
    c: Equal(g16,g17)
    c: Equal(g16,g18)
    c: InternalAlignment(g16,g19)
    c: InternalAlignment(g17,g19)
    c: InternalAlignment(g18,g19)
    c: InternalAlignment(g20,g19)
    c: InternalAlignment(g21,g19)
    c: Weight(g22) = 1
    c: Equal(g22,g23)
    c: Equal(g22,g24)
    c: InternalAlignment(g22,g25)
    c: InternalAlignment(g23,g25)
    c: InternalAlignment(g24,g25)
    c: InternalAlignment(g26,g25)
    c: InternalAlignment(g27,g25)
    c: Block(g25)
    c: Block(g19)
    c: Weight(g28) = 1
    c: Equal(g28,g29)
    c: Equal(g28,g30)
    c: InternalAlignment(g28,g31)
    c: InternalAlignment(g29,g31)
    c: InternalAlignment(g30,g31)
    c: InternalAlignment(g32,g31)
    c: InternalAlignment(g33,g31)
    c: Weight(g34) = 1
    c: Equal(g34,g35)
    c: Equal(g34,g36)
    c: InternalAlignment(g34,g37)
    c: InternalAlignment(g35,g37)
    c: InternalAlignment(g36,g37)
    c: InternalAlignment(g38,g37)
    c: InternalAlignment(g39,g37)
    c: Block(g37)
    c: Block(g31)
    c: Weight(g40) = 1
    c: Equal(g40,g41)
    c: Equal(g40,g42)
    c: InternalAlignment(g40,g43)
    c: InternalAlignment(g41,g43)
    c: InternalAlignment(g42,g43)
    c: InternalAlignment(g44,g43)
    c: InternalAlignment(g45,g43)
    c: Weight(g46) = 1
    c: Equal(g46,g47)
    c: Equal(g46,g48)
    c: InternalAlignment(g46,g49)
    c: InternalAlignment(g47,g49)
    c: InternalAlignment(g48,g49)
    c: InternalAlignment(g50,g49)
    c: InternalAlignment(g51,g49)
    c: Block(g43)
    c: Block(g49)
    c: Coincident(g52,g7)
    c: Coincident(g52,g6)
    c: Horizontal(g52)
    c: Distance(g52) = 450
    c: Coincident(g53,g7)
    c: Coincident(g53,g6)
    c: Horizontal(g53)
    c: Horizontal(g54)
    c: Coincident(g5,g54)
    c: Block(g54)
    c: Coincident(g1,g54)
    c: Weight(g55) = 1
    c: Equal(g55,g56)
    c: Equal(g55,g57)
    c: InternalAlignment(g55,g58)
    c: InternalAlignment(g56,g58)
    c: InternalAlignment(g57,g58)
    c: InternalAlignment(g59,g58)
    c: InternalAlignment(g60,g58)
    c: Block(g58)
    c: Weight(g61) = 1
    c: Equal(g61,g62)
    c: Equal(g61,g63)
    c: InternalAlignment(g61,g64)
    c: InternalAlignment(g62,g64)
    c: InternalAlignment(g63,g64)
    c: InternalAlignment(g65,g64)
    c: InternalAlignment(g66,g64)
    c: Block(g64)
    c: Weight(g67) = 1
    c: Equal(g67,g68)
    c: Equal(g67,g69)
    c: InternalAlignment(g67,g70)
    c: InternalAlignment(g68,g70)
    c: InternalAlignment(g69,g70)
    c: InternalAlignment(g71,g70)
    c: InternalAlignment(g72,g70)
    c: Block(g70)
    c: Weight(g73) = 1
    c: Equal(g73,g74)
    c: Equal(g73,g75)
    c: InternalAlignment(g73,g76)
    c: InternalAlignment(g74,g76)
    c: InternalAlignment(g75,g76)
    c: InternalAlignment(g77,g76)
    c: InternalAlignment(g78,g76)
    c: Block(g76)
    c: Weight(g79) = 1
    c: Equal(g79,g80)
    c: Equal(g79,g81)
    c: InternalAlignment(g79,g82)
    c: InternalAlignment(g80,g82)
    c: InternalAlignment(g81,g82)
    c: InternalAlignment(g83,g82)
    c: InternalAlignment(g84,g82)
    c: Weight(g85) = 1
    c: Equal(g85,g86)
    c: Equal(g85,g87)
    c: InternalAlignment(g85,g88)
    c: InternalAlignment(g86,g88)
    c: InternalAlignment(g87,g88)
    c: InternalAlignment(g89,g88)
    c: InternalAlignment(g90,g88)
    c: Block(g82)
    c: Block(g88)
    c: Coincident(g91,g82)
    c: Coincident(g91,g88)
    c: Vertical(g91)
    c: Coincident(g92,g82)
    c: Coincident(g92,g64)
    c: Coincident(g93,g64)
    c: Coincident(g93,g88)
    c: Weight(g94) = 1
    c: Equal(g94,g95)
    c: Equal(g94,g96)
    c: InternalAlignment(g94,g97)
    c: InternalAlignment(g95,g97)
    c: InternalAlignment(g96,g97)
    c: InternalAlignment(g98,g97)
    c: InternalAlignment(g99,g97)
    c: Weight(g100) = 1
    c: Equal(g100,g101)
    c: Equal(g100,g102)
    c: InternalAlignment(g100,g103)
    c: InternalAlignment(g101,g103)
    c: InternalAlignment(g102,g103)
    c: InternalAlignment(g104,g103)
    c: InternalAlignment(g105,g103)
    c: Block(g97)
    c: Block(g103)
    c: Coincident(g106,g97)
    c: Coincident(g106,g103)
    c: Vertical(g106)
    c: Coincident(g107,g97)
    c: Coincident(g107,g58)
    c: Coincident(g108,g58)
    c: Coincident(g108,g103)
    c: Weight(g109) = 1
    c: Equal(g109,g110)
    c: Equal(g109,g111)
    c: InternalAlignment(g109,g112)
    c: InternalAlignment(g110,g112)
    c: InternalAlignment(g111,g112)
    c: InternalAlignment(g113,g112)
    c: InternalAlignment(g114,g112)
    c: Weight(g115) = 1
    c: Equal(g115,g116)
    c: Equal(g115,g117)
    c: InternalAlignment(g115,g118)
    c: InternalAlignment(g116,g118)
    c: InternalAlignment(g117,g118)
    c: InternalAlignment(g119,g118)
    c: InternalAlignment(g120,g118)
    c: Block(g112)
    c: Block(g118)
    c: Coincident(g121,g112)
    c: Coincident(g121,g118)
    c: Vertical(g121)
    c: Coincident(g122,g118)
    c: Coincident(g122,g76)
    c: Coincident(g123,g76)
    c: Coincident(g123,g112)
    c: Weight(g124) = 1
    c: Equal(g124,g125)
    c: Equal(g124,g126)
    c: InternalAlignment(g124,g127)
    c: InternalAlignment(g125,g127)
    c: InternalAlignment(g126,g127)
    c: InternalAlignment(g128,g127)
    c: InternalAlignment(g129,g127)
    c: Weight(g130) = 1
    c: Equal(g130,g131)
    c: Equal(g130,g132)
    c: InternalAlignment(g130,g133)
    c: InternalAlignment(g131,g133)
    c: InternalAlignment(g132,g133)
    c: InternalAlignment(g134,g133)
    c: InternalAlignment(g135,g133)
    c: Block(g127)
    c: Block(g133)
    c: Coincident(g136,g127)
    c: Coincident(g136,g133)
    c: Vertical(g136)
    c: Coincident(g137,g133)
    c: Coincident(g137,g70)
    c: Coincident(g138,g70)
    c: Coincident(g138,g127)
    c: Weight(g139) = 1
    c: Equal(g139,g140)
    c: Equal(g139,g141)
    c: InternalAlignment(g139,g142)
    c: InternalAlignment(g140,g142)
    c: InternalAlignment(g141,g142)
    c: InternalAlignment(g143,g142)
    c: InternalAlignment(g144,g142)
    c: Weight(g145) = 1
    c: Equal(g145,g146)
    c: Equal(g145,g147)
    c: InternalAlignment(g145,g148)
    c: InternalAlignment(g146,g148)
    c: InternalAlignment(g147,g148)
    c: InternalAlignment(g149,g148)
    c: InternalAlignment(g150,g148)
    c: Weight(g151) = 1
    c: Equal(g151,g152)
    c: Equal(g151,g153)
    c: InternalAlignment(g151,g154)
    c: InternalAlignment(g152,g154)
    c: InternalAlignment(g153,g154)
    c: InternalAlignment(g155,g154)
    c: InternalAlignment(g156,g154)
    c: Weight(g157) = 1
    c: Equal(g157,g158)
    c: Equal(g157,g159)
    c: InternalAlignment(g157,g160)
    c: InternalAlignment(g158,g160)
    c: InternalAlignment(g159,g160)
    c: InternalAlignment(g161,g160)
    c: InternalAlignment(g162,g160)
    c: Block(g160)
    c: Block(g154)
    c: Block(g148)
    c: Block(g142)
    c: Coincident(g163,g37)
    c: Coincident(g163,g160)
    c: Coincident(g164,g160)
    c: Coincident(g164,g154)
    c: Horizontal(g164)
    c: Coincident(g165,g154)
    c: Coincident(g165,g37)
    c: Vertical(g165)
    c: Coincident(g166,g31)
    c: Coincident(g166,g148)
    c: Vertical(g166)
    c: Coincident(g167,g148)
    c: Coincident(g167,g142)
    c: Horizontal(g167)
    c: Coincident(g168,g142)
    c: Coincident(g168,g31)
    c: Weight(g169) = 1
    c: Equal(g169,g170)
    c: Equal(g169,g171)
    c: InternalAlignment(g169,g172)
    c: InternalAlignment(g170,g172)
    c: InternalAlignment(g171,g172)
    c: InternalAlignment(g173,g172)
    c: InternalAlignment(g174,g172)
    c: Weight(g175) = 1
    c: Equal(g175,g176)
    c: Equal(g175,g177)
    c: InternalAlignment(g175,g178)
    c: InternalAlignment(g176,g178)
    c: InternalAlignment(g177,g178)
    c: InternalAlignment(g179,g178)
    c: InternalAlignment(g180,g178)
    c: Weight(g181) = 1
    c: Equal(g181,g182)
    c: Equal(g181,g183)
    c: InternalAlignment(g181,g184)
    c: InternalAlignment(g182,g184)
    c: InternalAlignment(g183,g184)
    c: InternalAlignment(g185,g184)
    c: InternalAlignment(g186,g184)
    c: Weight(g187) = 1
    c: Equal(g187,g188)
    c: Equal(g187,g189)
    c: InternalAlignment(g187,g190)
    c: InternalAlignment(g188,g190)
    c: InternalAlignment(g189,g190)
    c: InternalAlignment(g191,g190)
    c: InternalAlignment(g192,g190)
    c: Block(g190)
    c: Block(g184)
    c: Block(g178)
    c: Block(g172)
    c: Coincident(g193,g190)
    c: Coincident(g193,g184)
    c: Horizontal(g193)
    c: Coincident(g194,g184)
    c: Coincident(g194,g19)
    c: Vertical(g194)
    c: Coincident(g195,g25)
    c: Coincident(g195,g178)
    c: Vertical(g195)
    c: Coincident(g196,g178)
    c: Coincident(g196,g172)
    c: Horizontal(g196)
    c: Coincident(g197,g172)
    c: Coincident(g197,g25)
    c: Coincident(g198,g19)
    c: Weight(g199) = 1
    c: Equal(g199,g200)
    c: Equal(g199,g201)
    c: InternalAlignment(g199,g202)
    c: InternalAlignment(g200,g202)
    c: InternalAlignment(g201,g202)
    c: InternalAlignment(g203,g202)
    c: InternalAlignment(g204,g202)
    c: Weight(g205) = 1
    c: Equal(g205,g206)
    c: Equal(g205,g207)
    c: InternalAlignment(g205,g208)
    c: InternalAlignment(g206,g208)
    c: InternalAlignment(g207,g208)
    c: InternalAlignment(g209,g208)
    c: InternalAlignment(g210,g208)
    c: Block(g208)
    c: Block(g202)
    c: Coincident(g211,g208)
    c: Coincident(g211,g43)
    c: Coincident(g212,g43)
    c: Coincident(g212,g202)
    c: Coincident(g213,g202)
    c: Coincident(g213,g208)
    c: Vertical(g213)
    c: Weight(g214) = 1
    c: Equal(g214,g215)
    c: Equal(g214,g216)
    c: InternalAlignment(g214,g217)
    c: InternalAlignment(g215,g217)
    c: InternalAlignment(g216,g217)
    c: InternalAlignment(g218,g217)
    c: InternalAlignment(g219,g217)
    c: Weight(g220) = 1
    c: Equal(g220,g221)
    c: Equal(g220,g222)
    c: InternalAlignment(g220,g223)
    c: InternalAlignment(g221,g223)
    c: InternalAlignment(g222,g223)
    c: InternalAlignment(g224,g223)
    c: InternalAlignment(g225,g223)
    c: Block(g223)
    c: Block(g217)
    c: Coincident(g226,g217)
    c: Coincident(g226,g49)
    c: Coincident(g227,g49)
    c: Coincident(g227,g223)
    c: Coincident(g228,g223)
    c: Coincident(g228,g217)
    c: Vertical(g228)
    c: Horizontal(g229)
    c: Block(g229)
    c: Vertical(g230)
    c: Block(g230)
    c: Block(g231)
    c: Weight(g232) = 1
    c: Equal(g232,g233)
    c: Equal(g232,g234)
    c: InternalAlignment(g232,g235)
    c: InternalAlignment(g233,g235)
    c: InternalAlignment(g234,g235)
    c: InternalAlignment(g236,g235)
    c: InternalAlignment(g237,g235)
    c: Weight(g238) = 1
    c: Equal(g238,g239)
    c: Equal(g238,g240)
    c: InternalAlignment(g238,g241)
    c: InternalAlignment(g239,g241)
    c: InternalAlignment(g240,g241)
    c: InternalAlignment(g242,g241)
    c: InternalAlignment(g243,g241)
    c: Weight(g244) = 1
    c: Equal(g244,g245)
    c: Equal(g244,g246)
    c: InternalAlignment(g244,g247)
    c: InternalAlignment(g245,g247)
    c: InternalAlignment(g246,g247)
    c: InternalAlignment(g248,g247)
    c: InternalAlignment(g249,g247)
    c: Weight(g250) = 1
    c: Equal(g250,g251)
    c: Equal(g250,g252)
    c: InternalAlignment(g250,g253)
    c: InternalAlignment(g251,g253)
    c: InternalAlignment(g252,g253)
    c: InternalAlignment(g254,g253)
    c: InternalAlignment(g255,g253)
    c: Block(g235)
    c: Block(g241)
    c: Block(g247)
    c: Block(g253)
    c: Coincident(g256,g241)
    c: Coincident(g256,g235)
    c: Horizontal(g256)
    c: Block(g198)
    c: Weight(g257) = 1
    c: Equal(g257,g258)
    c: Equal(g257,g259)
    c: InternalAlignment(g257,g260)
    c: InternalAlignment(g258,g260)
    c: InternalAlignment(g259,g260)
    c: InternalAlignment(g261,g260)
    c: InternalAlignment(g262,g260)
    c: Weight(g263) = 1
    c: Equal(g263,g264)
    c: Equal(g263,g265)
    c: InternalAlignment(g263,g266)
    c: InternalAlignment(g264,g266)
    c: InternalAlignment(g265,g266)
    c: InternalAlignment(g267,g266)
    c: InternalAlignment(g268,g266)
    c: Weight(g269) = 1
    c: Equal(g269,g270)
    c: Equal(g269,g271)
    c: InternalAlignment(g269,g272)
    c: InternalAlignment(g270,g272)
    c: InternalAlignment(g271,g272)
    c: InternalAlignment(g273,g272)
    c: InternalAlignment(g274,g272)
    c: Weight(g275) = 1
    c: Equal(g275,g276)
    c: Equal(g275,g277)
    c: InternalAlignment(g275,g278)
    c: InternalAlignment(g276,g278)
    c: InternalAlignment(g277,g278)
    c: InternalAlignment(g279,g278)
    c: InternalAlignment(g280,g278)
    c: Block(g260)
    c: Block(g266)
    c: Block(g272)
    c: Block(g278)
    c: Coincident(g281,g272)
    c: Coincident(g281,g278)
    c: Horizontal(g281)
    c: Coincident(g282,g278)
    c: Coincident(g282,g260)
    c: Vertical(g282)
    c: Coincident(g283,g260)
    c: Coincident(g283,g266)
    c: Coincident(g284,g266)
    c: Coincident(g284,g272)
    c: Vertical(g284)
    c: Weight(g285) = 1
    c: Equal(g285,g286)
    c: Equal(g285,g287)
    c: InternalAlignment(g285,g288)
    c: InternalAlignment(g286,g288)
    c: InternalAlignment(g287,g288)
    c: InternalAlignment(g289,g288)
    c: InternalAlignment(g290,g288)
    c: Weight(g291) = 1
    c: Equal(g291,g292)
    c: Equal(g291,g293)
    c: InternalAlignment(g291,g294)
    c: InternalAlignment(g292,g294)
    c: InternalAlignment(g293,g294)
    c: InternalAlignment(g295,g294)
    c: InternalAlignment(g296,g294)
    c: Weight(g297) = 1
    c: Equal(g297,g298)
    c: Equal(g297,g299)
    c: InternalAlignment(g297,g300)
    c: InternalAlignment(g298,g300)
    c: InternalAlignment(g299,g300)
    c: InternalAlignment(g301,g300)
    c: InternalAlignment(g302,g300)
    c: Block(g300)
    c: Block(g294)
    c: Block(g288)
    c: Coincident(g303,g294)
    c: Coincident(g303,g288)
    c: Coincident(g304,g288)
    c: Coincident(g304,g300)
    c: Vertical(g304)
    c: Coincident(g305,g300)
    c: Coincident(g305,g294)
    c: Horizontal(g305)
    c: Weight(g306) = 1
    c: Equal(g306,g307)
    c: InternalAlignment(g306,g308)
    c: InternalAlignment(g307,g308)
    c: InternalAlignment(g309,g308)
    c: InternalAlignment(g310,g308)
    c: Weight(g311) = 1
    c: Equal(g311,g312)
    c: Equal(g311,g313)
    c: InternalAlignment(g311,g314)
    c: InternalAlignment(g312,g314)
    c: InternalAlignment(g313,g314)
    c: InternalAlignment(g315,g314)
    c: InternalAlignment(g316,g314)
    c: Weight(g317) = 1
    c: Equal(g317,g318)
    c: Equal(g317,g319)
    c: InternalAlignment(g317,g320)
    c: InternalAlignment(g318,g320)
    c: InternalAlignment(g319,g320)
    c: InternalAlignment(g321,g320)
    c: InternalAlignment(g322,g320)
    c: Equal(g323,g324)
    c: Equal(g323,g325)
    c: InternalAlignment(g323,g326)
    c: InternalAlignment(g324,g326)
    c: InternalAlignment(g325,g326)
    c: InternalAlignment(g327,g326)
    c: InternalAlignment(g328,g326)
    c: Block(g314)
    c: Block(g320)
    c: Block(g326)
    c: Block(g308)
    c: Coincident(g329,g308)
    c: Coincident(g329,g314)
    c: Horizontal(g329)
    c: Coincident(g330,g314)
    c: Coincident(g330,g320)
    c: Vertical(g330)
    c: Coincident(g331,g320)
    c: Coincident(g331,g326)
    c: Horizontal(g331)
    c: Coincident(g332,g326)
    c: Coincident(g332,g308)
    c: Vertical(g333)
    c: Vertical(g334)
    c: Horizontal(g335)
    c: Horizontal(g336)
FEATURE [Sketcher::SketchObject] Sketch001
  FullyConstrained = true
  MapMode = 4
  Placement = pos=(0,0,0) rot=(0.57735,0.57735,0.57735;2.0944rad)
  Support = -> [Sketch]
  sketch-geometry (46):
    g0: BSplineCurve PolesCount=3 KnotsCount=2 Degree=2 IsPeriodic=0
    g1: ArcOfCircle CenterX=73.1223 CenterY=-32.291 CenterZ=0 NormalX=0 NormalY=0 NormalZ=1 AngleXU=0 Radius=13 StartAngle=5.92268 EndAngle=9.06428
    g2: ArcOfCircle CenterX=66.7816 CenterY=-49.1439 CenterZ=0 NormalX=0 NormalY=0 NormalZ=1 AngleXU=0 Radius=13 StartAngle=2.78068 EndAngle=5.92131
    g3: ArcOfCircle CenterX=55.9263 CenterY=-78.1807 CenterZ=0 NormalX=0 NormalY=0 NormalZ=1 AngleXU=0 Radius=13 StartAngle=5.92268 EndAngle=9.06428
    g4: ArcOfCircle CenterX=49.5884 CenterY=-95.0342 CenterZ=0 NormalX=0 NormalY=0 NormalZ=1 AngleXU=0 Radius=13 StartAngle=2.78068 EndAngle=5.92131
    g5: ArcOfCircle CenterX=38.7206 CenterY=-124.067 CenterZ=0 NormalX=0 NormalY=0 NormalZ=1 AngleXU=0 Radius=13 StartAngle=5.92268 EndAngle=9.06428
    g6: ArcOfCircle CenterX=32.3875 CenterY=-140.92 CenterZ=0 NormalX=0 NormalY=0 NormalZ=1 AngleXU=0 Radius=13 StartAngle=2.78068 EndAngle=5.92131
    g7: ArcOfCircle CenterX=21.4715 CenterY=-169.934 CenterZ=0 NormalX=0 NormalY=0 NormalZ=1 AngleXU=0 Radius=13 StartAngle=5.92268 EndAngle=9.06428
    g8: ArcOfCircle CenterX=15.1336 CenterY=-186.787 CenterZ=0 NormalX=0 NormalY=0 NormalZ=1 AngleXU=0 Radius=13 StartAngle=2.78068 EndAngle=5.92131
    g9-g12: Circle x4 (B-spline internal-alignment scaffolding for g13; pole/knot coordinates omitted)
    g13: BSplineCurve PolesCount=4 KnotsCount=2 Degree=3 IsPeriodic=0
    g14: GeomPoint X=28.8094 Y=-19.0875 Z=0
    g15: GeomPoint X=47.0443 Y=-50.4712 Z=0
    g16: Circle CenterX=53.5586 CenterY=-23.2695 CenterZ=0 NormalX=0 NormalY=0 NormalZ=1 AngleXU=0 Radius=3.24518
    g17: Circle CenterX=-195.441 CenterY=-127.082 CenterZ=0 NormalX=0 NormalY=0 NormalZ=1 AngleXU=0 Radius=1
    g18: Circle CenterX=-8.24091 CenterY=-197.481 CenterZ=0 NormalX=0 NormalY=0 NormalZ=1 AngleXU=0 Radius=1
    g19: Circle CenterX=12.8789 CenterY=-141.321 CenterZ=0 NormalX=0 NormalY=0 NormalZ=1 AngleXU=0 Radius=1
    g20: BSplineCurve PolesCount=3 KnotsCount=2 Degree=2 IsPeriodic=0
    g21: GeomPoint X=-195.441 Y=-127.082 Z=0
    g22: GeomPoint X=12.8789 Y=-141.321 Z=0
    g23: Circle CenterX=-12.8016 CenterY=-179.036 CenterZ=0 NormalX=0 NormalY=0 NormalZ=1 AngleXU=0 Radius=10.5072
    g24: Circle CenterX=0.933922 CenterY=-166.43 CenterZ=0 NormalX=0 NormalY=0 NormalZ=1 AngleXU=0 Radius=3.26661
    g25: Circle CenterX=-33.5518 CenterY=-176.44 CenterZ=0 NormalX=0 NormalY=0 NormalZ=1 AngleXU=0 Radius=5.64388
    g26: Circle CenterX=-47.2366 CenterY=-173.859 CenterZ=0 NormalX=0 NormalY=0 NormalZ=1 AngleXU=0 Radius=3.01653
    g27: Circle CenterX=-56.2595 CenterY=-171.456 CenterZ=0 NormalX=0 NormalY=0 NormalZ=1 AngleXU=0 Radius=2.12826
    g28: ArcOfCircle CenterX=51.2151 CenterY=-198.473 CenterZ=0 NormalX=0 NormalY=0 NormalZ=1 AngleXU=0 Radius=20 StartAngle=2.78189 EndAngle=4.35269
    g29: LineSegment StartX=32.4951 StartY=-191.433 StartZ=0 EndX=94.6578 EndY=-26.1352 EndZ=0
    g30: LineSegment StartX=43.1192 StartY=-220.001 StartZ=0 EndX=-196.497 EndY=-129.89 EndZ=0
    g31: LineSegment StartX=43.1192 StartY=-220.001 StartZ=0 EndX=44.1752 EndY=-217.193 EndZ=0
    g32: LineSegment StartX=117.223 StartY=-19.0875 StartZ=0 EndX=117.223 EndY=-16.0875 EndZ=0
    g33: LineSegment StartX=117.223 StartY=-16.0875 StartZ=0 EndX=17.2232 EndY=-16.0875 EndZ=0
    g34: LineSegment StartX=17.2232 StartY=-16.0875 StartZ=0 EndX=17.2232 EndY=-19.0875 EndZ=0
    g35: LineSegment StartX=28.8094 StartY=-19.0875 StartZ=0 EndX=17.2232 EndY=-19.0875 EndZ=0
    g36: LineSegment StartX=47.0443 StartY=-50.4712 StartZ=0 EndX=12.8789 EndY=-141.321 EndZ=0
    g37: LineSegment StartX=-195.441 StartY=-127.082 StartZ=0 EndX=-196.497 EndY=-129.89 EndZ=0
    g38: LineSegment StartX=85.2866 StartY=-36.8766 StartZ=0 EndX=78.9396 EndY=-53.7463 EndZ=0
    g39: LineSegment StartX=60.9579 StartY=-27.7053 StartZ=0 EndX=54.6191 EndY=-44.5532 EndZ=0
    g40: LineSegment StartX=68.0907 StartY=-82.7664 StartZ=0 EndX=61.7465 EndY=-99.6365 EndZ=0
    g41: LineSegment StartX=43.7619 StartY=-73.595 StartZ=0 EndX=37.426 EndY=-90.4435 EndZ=0
    g42: LineSegment StartX=50.885 StartY=-128.652 StartZ=0 EndX=44.5456 EndY=-145.522 EndZ=0
    g43: LineSegment StartX=26.5562 StartY=-119.481 StartZ=0 EndX=20.2251 EndY=-136.329 EndZ=0
    g44: LineSegment StartX=9.3071 StartY=-165.349 StartZ=0 EndX=2.97115 EndY=-182.197 EndZ=0
    g45: LineSegment StartX=33.6358 StartY=-174.52 StartZ=0 EndX=27.2917 EndY=-191.39 EndZ=0
  constraints (71):
    c: Block(g0)
    c: Block(g1)
    c: Block(g2)
    c: Block(g4)
    c: Block(g3)
    c: Block(g6)
    c: Block(g5)
    c: Block(g8)
    c: Block(g7)
    c: Weight(g9) = 1
    c: Equal(g9,g10)
    c: Equal(g9,g11)
    c: Equal(g9,g12)
    c: InternalAlignment(g9-g12 -> g13) x4
    c: InternalAlignment(g14,g13)
    c: InternalAlignment(g15,g13)
    c: Block(g16)
    c: Weight(g17) = 1
    c: Equal(g17,g18)
    c: Equal(g17,g19)
    c: InternalAlignment(g17,g20)
    c: InternalAlignment(g18,g20)
    c: InternalAlignment(g19,g20)
    c: InternalAlignment(g21,g20)
    c: InternalAlignment(g22,g20)
    c: Block(g20)
    c: Block(g23)
    c: Block(g24)
    c: Block(g25)
    c: Block(g26)
    c: Block(g27)
    c: Block(g28)
    c: Coincident(g29,g28)
    c: Coincident(g29,g0)
    c: Block(g13)
    c: Coincident(g31,g30)
    c: Coincident(g31,g28)
    c: Block(g31)
    c: Coincident(g32,g0)
    c: Vertical(g32)
    c: Coincident(g33,g32)
    c: Horizontal(g33)
    c: Coincident(g34,g33)
    c: Vertical(g34)
    c: Block(g33)
    c: Coincident(g35,g13)
    c: Coincident(g35,g34)
    c: Horizontal(g35)
    c: Coincident(g36,g13)
    c: Coincident(g36,g20)
    c: Coincident(g37,g20)
    c: Coincident(g37,g30)
    c: Block(g30)
    c: Coincident(g38,g1)
    c: Coincident(g38,g2)
    c: Coincident(g39,g1)
    c: Coincident(g39,g2)
    c: Coincident(g40,g3)
    c: Coincident(g40,g4)
    c: Coincident(g41,g3)
    c: Coincident(g41,g4)
    c: Coincident(g42,g5)
    c: Coincident(g42,g6)
    c: Coincident(g43,g5)
    c: Coincident(g43,g6)
    c: Coincident(g44,g7)
    c: Coincident(g44,g8)
    c: Coincident(g45,g7)
    c: Coincident(g45,g8)
    c: Distance(g30) = 256
    c: Distance(g33) = 100
FEATURE [Part::Extrusion] Extrude002
  Base = -> Sketch001
  Dir = (1,0,0)
  DirMode = 2
  FaceMakerClass = Part::FaceMakerBullseye
  LengthFwd = 8
  LengthRev = 0
  Solid = true
  Symmetric = false
FEATURE [Sketcher::SketchObject] Sketch002
  FullyConstrained = true
  sketch-geometry (20):
    g0: LineSegment StartX=-2.77179 StartY=-200.304 StartZ=0 EndX=5.22821 EndY=-200.304 EndZ=0
    g1: LineSegment StartX=5.22821 StartY=-200.304 StartZ=0 EndX=5.22821 EndY=-197.304 EndZ=0
    g2: LineSegment StartX=-2.77179 StartY=-200.304 StartZ=0 EndX=-2.77179 EndY=-197.304 EndZ=0
    g3: LineSegment StartX=5.22821 StartY=-197.304 StartZ=0 EndX=8.22821 EndY=-197.304 EndZ=0
    g4: LineSegment StartX=-2.77179 StartY=-197.304 StartZ=0 EndX=-5.77179 EndY=-197.304 EndZ=0
    g5: LineSegment StartX=19.2282 StartY=-203.304 StartZ=0 EndX=19.2282 EndY=-206.304 EndZ=0
    g6: LineSegment StartX=-16.7718 StartY=-203.304 StartZ=0 EndX=-16.7718 EndY=-206.304 EndZ=0
    g7: LineSegment StartX=-16.7718 StartY=-206.304 StartZ=0 EndX=19.2282 EndY=-206.304 EndZ=0
    g8: Circle CenterX=-16.7718 CenterY=-203.304 CenterZ=0 NormalX=0 NormalY=0 NormalZ=1 AngleXU=0 Radius=1
    g9: Circle CenterX=-5.77179 CenterY=-203.304 CenterZ=0 NormalX=0 NormalY=0 NormalZ=1 AngleXU=0 Radius=1
    g10: Circle CenterX=-5.77179 CenterY=-197.304 CenterZ=0 NormalX=0 NormalY=0 NormalZ=1 AngleXU=0 Radius=1
    g11: BSplineCurve PolesCount=3 KnotsCount=2 Degree=2 IsPeriodic=0
    g12: GeomPoint X=-16.7718 Y=-203.304 Z=0
    g13: GeomPoint X=-5.77179 Y=-197.304 Z=0
    g14: Circle CenterX=19.2282 CenterY=-203.304 CenterZ=0 NormalX=0 NormalY=0 NormalZ=1 AngleXU=0 Radius=1
    g15: Circle CenterX=8.22821 CenterY=-203.304 CenterZ=0 NormalX=0 NormalY=0 NormalZ=1 AngleXU=0 Radius=1
    g16: Circle CenterX=8.22821 CenterY=-197.304 CenterZ=0 NormalX=0 NormalY=0 NormalZ=1 AngleXU=0 Radius=1
    g17: BSplineCurve PolesCount=3 KnotsCount=2 Degree=2 IsPeriodic=0
    g18: GeomPoint X=19.2282 Y=-203.304 Z=0
    g19: GeomPoint X=8.22821 Y=-197.304 Z=0
  constraints (41):
    c: Horizontal(g0)
    c: Distance(g0) = 8
    c: Coincident(g1,g0)
    c: Vertical(g1)
    c: Distance(g1) = 3
    c: Coincident(g2,g0)
    c: Vertical(g2)
    c: Distance(g2) = 3
    c: Coincident(g3,g1)
    c: Horizontal(g3)
    c: Distance(g3) = 3
    c: Coincident(g4,g2)
    c: Horizontal(g4)
    c: Distance(g4) = 3
    c: Vertical(g5)
    c: Vertical(g6)
    c: Coincident(g7,g6)
    c: Coincident(g7,g5)
    c: Weight(g8) = 1
    c: Equal(g8,g9)
    c: Equal(g8,g10)
    c: Coincident(g11,g4)
    c: InternalAlignment(g8,g11)
    c: InternalAlignment(g9,g11)
    c: InternalAlignment(g10,g11)
    c: InternalAlignment(g12,g11)
    c: InternalAlignment(g13,g11)
    c: Coincident(g17,g5)
    c: Weight(g14) = 1
    c: Equal(g14,g15)
    c: Equal(g14,g16)
    c: Coincident(g17,g3)
    c: InternalAlignment(g14,g17)
    c: InternalAlignment(g15,g17)
    c: InternalAlignment(g16,g17)
    c: InternalAlignment(g18,g17)
    c: InternalAlignment(g19,g17)
    c: Block(g7)
    c: Block(g17)
    c: Block(g11)
    c: Block(g6)
FEATURE [Part::Extrusion] Extrude003
  Base = -> Sketch002
  Dir = (0,0,1)
  DirMode = 2
  FaceMakerClass = Part::FaceMakerBullseye
  LengthFwd = 260
  LengthRev = 0
  Solid = true
  Symmetric = false
FEATURE [Part::Extrusion] Extrude
  Base = -> Sketch
  Dir = (0,0,1)
  DirMode = 2
  FaceMakerClass = Part::FaceMakerBullseye
  LengthFwd = 14
  LengthRev = 0
  Solid = true
  Symmetric = false
